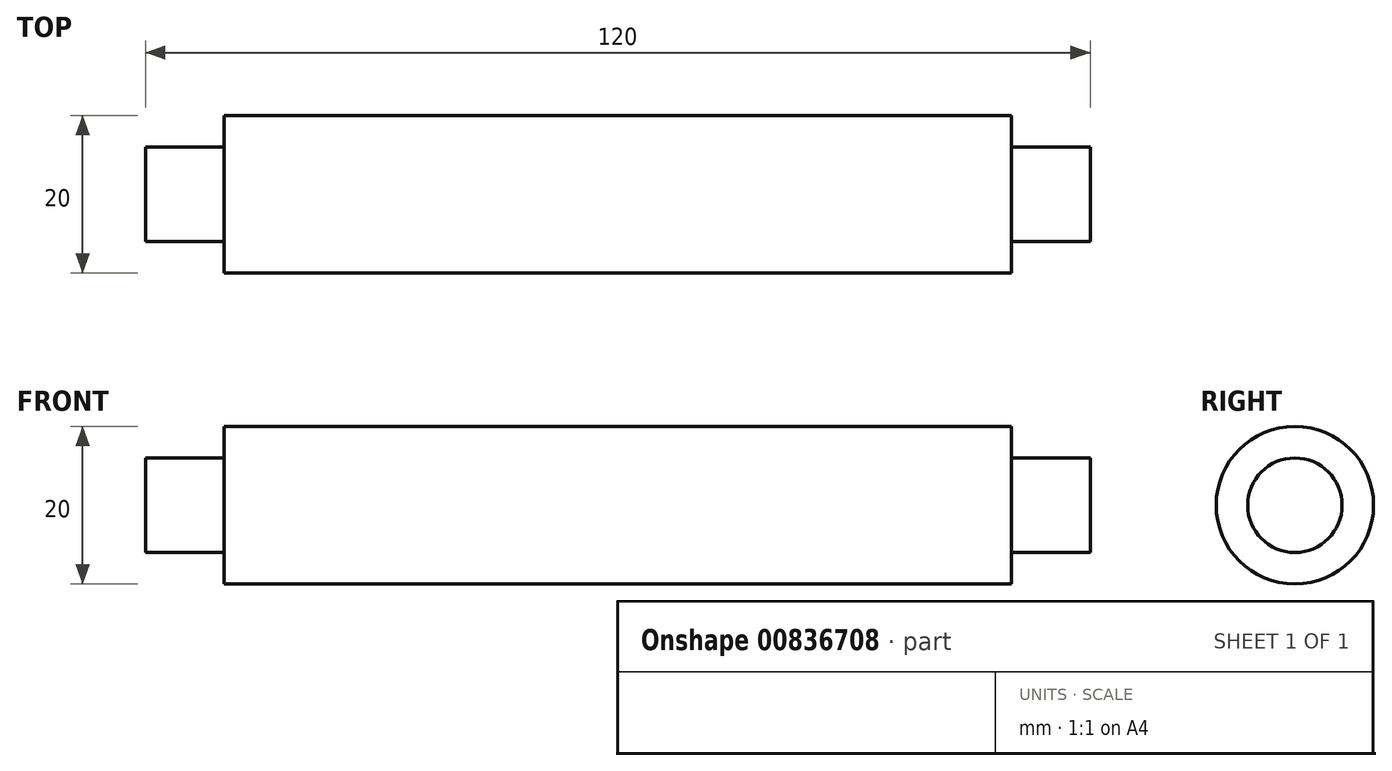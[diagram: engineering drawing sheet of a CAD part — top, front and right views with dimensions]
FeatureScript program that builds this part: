
annotation { "Feature Type Name" : "Feature", "Feature Type Description" : "" }
export const myFeature = defineFeature(function(context is Context, id is Id, definition is map)
    precondition{}
    {
        {
            var Q0;
            Q0=qCreatedBy(makeId("Front.planeOp"),FACE);
            var sketch = newSketch(context, id + "F0", { "sketchPlane" : qUnion([Q0])});
            skLineSegment(sketch, "E0.bottom", {"start": v(50, 5) * mm, "end": v(-50, 5) * mm});
            skLineSegment(sketch, "E0.top", {"start": v(50, -5) * mm, "end": v(-50, -5) * mm});
            skLineSegment(sketch, "E0.left", {"start": v(50, 5) * mm, "end": v(50, -5) * mm});
            skLineSegment(sketch, "E0.right", {"start": v(-50, 5) * mm, "end": v(-50, -5) * mm});
            skPoint(sketch, "E0.middle", {"position": v(0, 0) * mm});
            skLineSegment(sketch, "E1.bottom", {"start": v(-50, -5) * mm, "end": v(-60, -5) * mm});
            skLineSegment(sketch, "E1.top", {"start": v(-50, 1) * mm, "end": v(-60, 1) * mm});
            skLineSegment(sketch, "E1.left", {"start": v(-50, -5) * mm, "end": v(-50, 1) * mm});
            skLineSegment(sketch, "E1.right", {"start": v(-60, -5) * mm, "end": v(-60, 1) * mm});
            skLineSegment(sketch, "E2.bottom", {"start": v(50, -5) * mm, "end": v(60, -5) * mm});
            skLineSegment(sketch, "E2.top", {"start": v(50, 1) * mm, "end": v(60, 1) * mm});
            skLineSegment(sketch, "E2.left", {"start": v(50, -5) * mm, "end": v(50, 1) * mm});
            skLineSegment(sketch, "E2.right", {"start": v(60, -5) * mm, "end": v(60, 1) * mm});
            skSolve(sketch);
        }
        {
            var Q0;
            Q0 = qSketchRegion(id + "F0", true);
            var Q1;
            Q1=sQuery(id+"F0.wireOp",EDGE,"E0.top");
            revolve(context, id + "F1", {"surfaceOperationType" : NewSurfaceOperationType.NEW, "entities" : qUnion([Q0]), "axis" : qUnion([Q1]), "revolveType" : RevolveType.FULL});
        }
    });
